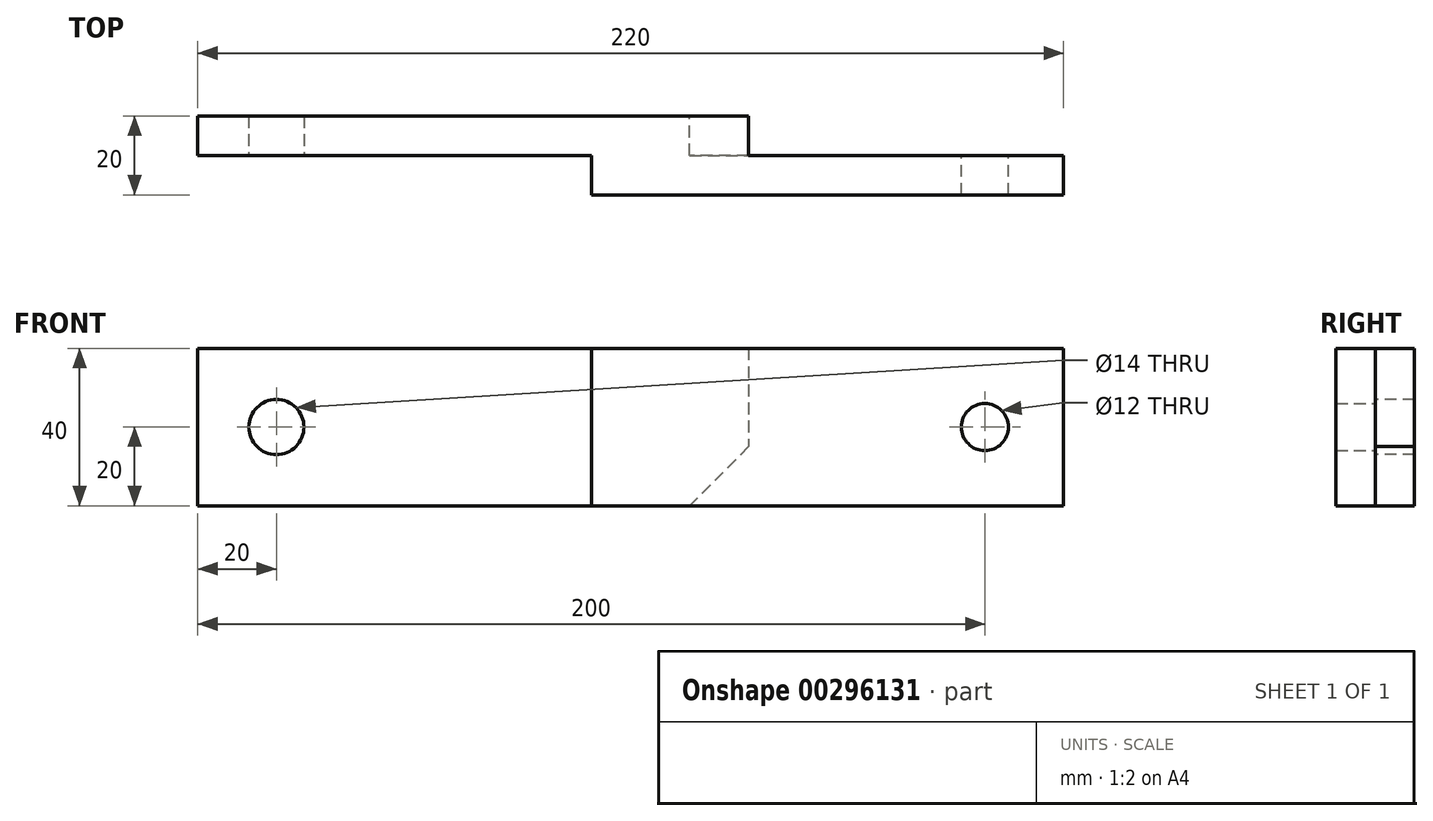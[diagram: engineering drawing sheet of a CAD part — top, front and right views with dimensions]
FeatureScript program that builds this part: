
annotation { "Feature Type Name" : "Feature", "Feature Type Description" : "" }
export const myFeature = defineFeature(function(context is Context, id is Id, definition is map)
    precondition{}
    {
        {
            var Q0;
            Q0=qCreatedBy(makeId("Right.planeOp"),FACE);
            var sketch = newSketch(context, id + "F0", { "sketchPlane" : qUnion([Q0])});
            skLineSegment(sketch, "E0.bottom", {"start": v(5, 20) * mm, "end": v(-5, 20) * mm});
            skLineSegment(sketch, "E0.top", {"start": v(5, -20) * mm, "end": v(-5, -20) * mm});
            skLineSegment(sketch, "E0.left", {"start": v(5, 20) * mm, "end": v(5, -20) * mm});
            skLineSegment(sketch, "E0.right", {"start": v(-5, 20) * mm, "end": v(-5, -20) * mm});
            skPoint(sketch, "E0.middle", {"position": v(0, 0) * mm});
            skSolve(sketch);
        }
        {
            var Q0;
            Q0=makeQuery(id+"F0.imprint","IMPRINT",FACE,{"disambiguationData":[TD([[makeQuery(id+"F0.imprint","IMPRINT",EDGE,{"derivedFrom":sQuery(id+"F0.wireOp",EDGE,"E0.bottom")}),1.0]])]});
            extrude(context, id + "F1", {"entities" : qUnion([Q0]), "oppositeDirection" : true, "depth" : 140 * mm});
        }
        {
            var Q0;
            Q0=makeQuery(id+"F1.opExtrude","SWEPT_FACE",FACE,{"disambiguationData":[OSD([sQuery(id+"F0.wireOp",EDGE,"E0.right")])]});
            var sketch = newSketch(context, id + "F2", { "sketchPlane" : qUnion([Q0])});
            skLineSegment(sketch, "E1", {"start": v(-140, 0) * mm, "end": v(0, 0) * mm, "construction": true});
            skCircle(sketch, "E2", {"center": v(-120, 0) * mm, "radius": 7 * mm});
            skSolve(sketch);
        }
        {
            var Q0;
            Q0=makeQuery(id+"F2.imprint","IMPRINT",FACE,{"disambiguationData":[TD([[makeQuery(id+"F2.imprint","IMPRINT",EDGE,{"derivedFrom":sQuery(id+"F2.wireOp",EDGE,"E2")}),1.0]])]});
            var Q1;
            Q1=makeQuery(id+"F2.imprint","IMPRINT",FACE,{"disambiguationData":[TD([[makeQuery(id+"F2.imprint","IMPRINT",EDGE,{"derivedFrom":sQuery(id+"F2.wireOp",EDGE,"hCp7N3eA-Js92-YmUs-VyuM-hG2jx43pWJxT")}),1.0]])]});
            extrude(context, id + "F3", {"entities" : qUnion([Q0, Q1]), "operationType" : NewBodyOperationType.REMOVE, "endBound" : BoundingType.THROUGH_ALL, "oppositeDirection" : true, "depth" : 25 * mm});
        }
        {
            var Q0;
            Q0=makeQuery(id+"F1.opExtrude","SWEPT_FACE",FACE,{"disambiguationData":[OSD([sQuery(id+"F0.wireOp",EDGE,"E0.right")])]});
            var sketch = newSketch(context, id + "F4", { "sketchPlane" : qUnion([Q0])});
            skLineSegment(sketch, "E3.bottom", {"start": v(-40, 20) * mm, "end": v(80, 20) * mm});
            skLineSegment(sketch, "E3.top", {"start": v(-40, -20) * mm, "end": v(80, -20) * mm});
            skLineSegment(sketch, "E3.left", {"start": v(-40, 20) * mm, "end": v(-40, -20) * mm});
            skLineSegment(sketch, "E3.right", {"start": v(80, 20) * mm, "end": v(80, -20) * mm});
            skLineSegment(sketch, "E4", {"start": v(80, 0) * mm, "end": v(-40, 0) * mm, "construction": true});
            skCircle(sketch, "E5", {"center": v(60, 0) * mm, "radius": 6 * mm});
            skLineSegment(sketch, "E6", {"start": v(-40, 20) * mm, "end": v(-27.5, 20) * mm, "construction": true});
            skLineSegment(sketch, "E7", {"start": v(-40, 20) * mm, "end": v(-40, 9.52) * mm, "construction": true});
            skSolve(sketch);
        }
        {
            var Q0;
            Q0=makeQuery(id+"F4.imprint","IMPRINT",FACE,{"disambiguationData":[TD([[makeQuery(id+"F4.imprint","IMPRINT",EDGE,{"derivedFrom":sQuery(id+"F4.wireOp",EDGE,"mLdeGfp8-pvMP-BBXk-zaqC-qGqNJqb4OPHf.bottom")}),-1.0]])]});
            var Q1;
            {var subQ2=sQuery(id+"F4.wireOp",EDGE,"E3.right");Q1=makeQuery(id+"F4.imprint","IMPRINT",FACE,{"disambiguationData":[TD([[makeQuery(id+"F4.imprint","IMPRINT",EDGE,{"derivedFrom":subQ2}),-1.0]])]});}
            var Q2;
            {var subQ4=sQuery(id+"F4.wireOp",EDGE,"Fk4OIXwN-B3kw-eu3v-LkCD-ADhxMi3JoqQV");Q2=makeQuery(id+"F4.imprint","IMPRINT",FACE,{"disambiguationData":[TD([[makeQuery(id+"F4.imprint","IMPRINT",EDGE,{"derivedFrom":subQ4}),-1.0]])]});}
            var Q3;
            {var subQ3=sQuery(id+"F4.wireOp",EDGE,"E3.left");Q3=makeQuery(id+"F4.imprint","IMPRINT",FACE,{"disambiguationData":[TD([[makeQuery(id+"F4.imprint","IMPRINT",EDGE,{"derivedFrom":subQ3}),1.0]])]});}
            extrude(context, id + "F5", {"entities" : qUnion([Q0, Q1, Q2, Q3]), "operationType" : NewBodyOperationType.ADD, "depth" : 10 * mm});
        }
        {
            var Q0;
            Q0=makeQuery(id+"F1.opExtrude","SWEPT_FACE",FACE,{"disambiguationData":[OSD([sQuery(id+"F0.wireOp",EDGE,"E0.left")])]});
            var sketch = newSketch(context, id + "F6", { "sketchPlane" : qUnion([Q0])});
            skLineSegment(sketch, "E8", {"start": v(0, -20) * mm, "end": v(15, -20) * mm, "construction": true});
            skLineSegment(sketch, "E9", {"start": v(0, -20) * mm, "end": v(0, -5) * mm, "construction": true});
            skLineSegment(sketch, "E10", {"start": v(0, -5) * mm, "end": v(15, -20) * mm});
            skSolve(sketch);
        }
        {
            var Q0;
            {var subQ0=sQuery(id+"F6.wireOp",EDGE,"E10");Q0=makeQuery(id+"F6.imprint","IMPRINT",FACE,{"disambiguationData":[TD([[makeQuery(id+"F6.imprint","IMPRINT",EDGE,{"derivedFrom":subQ0}),-1.0]])]});}
            var Q1;
            Q1=makeQuery(id+"F5.opExtrude","CAP_FACE",FACE,{"disambiguationData":[OSD([sQuery(id+"F4.wireOp",EDGE,"E3.bottom"),sQuery(id+"F4.wireOp",EDGE,"E3.top"),sQuery(id+"F4.wireOp",EDGE,"E3.left"),sQuery(id+"F4.wireOp",EDGE,"E3.right"),sQuery(id+"F4.wireOp",EDGE,"E5"),sQuery(id+"F4.wireOp",EDGE,"Fk4OIXwN-B3kw-eu3v-LkCD-ADhxMi3JoqQV")])],"isStart":true});
            extrude(context, id + "F7", {"entities" : qUnion([Q0]), "operationType" : NewBodyOperationType.REMOVE, "endBound" : BoundingType.UP_TO_SURFACE, "oppositeDirection" : true, "endBoundEntityFace" : qUnion([Q1]), "depth" : 25 * mm});
        }
    });
